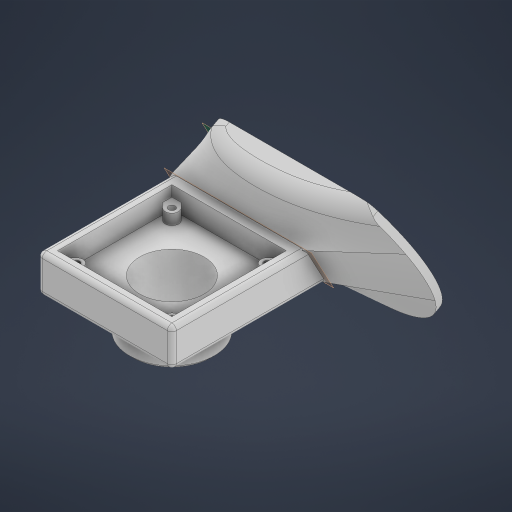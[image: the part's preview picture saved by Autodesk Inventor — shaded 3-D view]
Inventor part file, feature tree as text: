
AUTODESK INVENTOR PART (.ipt)
format: ipt  version: 2023 (Build 270158000, 158)  size: 586,752 bytes
history: native  units: in
note: dims shown in document units (in); Inventor stores cm internally (conversion verified against a paired STEP export)
features: sketch x10, extrude x7, hole x3, fillet x3, plane x2, chamfer x2, other x2, projected_geometry x2, loft x1
ambient origin geometry x8: Origin, YZ Plane, XZ Plane, XY Plane, X Axis, Y Axis, Z Axis, Center Point
bodies: Solid1 (feature_tree)
feature tree (32):
  extrude  "Extrusion1"  Depth=0.525in
  extrude  "Extrusion2"  Depth=0.4252in
  plane  "Work Plane1"
  extrude  "Extrusion3"  Depth=0.6in
  loft  "Loft1"
  extrude  "Extrusion4"  TaperAngle=0.0deg  [1 undecoded]
  hole  "Hole1"  [1 undecoded]
  extrude  "Extrusion5"  Depth=1.1875in
  extrude  "Extrusion6"  Depth=0.1839in
  hole  "Hole2"  [1 undecoded]
  plane  "Work Plane2"
  hole  "Hole3"  [1 undecoded]
  fillet  "Fillet1"  Radius=0.9792in
  chamfer  "Chamfer1"  Distance=0.4466in
  fillet  "Fillet2"  Radius=0.4in
  extrude  "Extrusion7"  Depth=0.15in
  fillet  "Fillet3"  Radius=0.0625in
  chamfer  "Chamfer2"  Distance=0.05in Angle=45.0deg
  sketch  "Sketch1"  dims[d0=1.875in d1=0.525in]
  sketch  "Sketch2"  dims[d2=1.875in d3=0.0in d4=0.4252in]
  sketch  "Sketch3"  dims[d5=1.875in d6=0.0in d7=0.6in]
  other  "Edges1"
  other  "Edges2"
  sketch  "Sketch4"  dims[d9=2.875in d10=0.1in d11=0.0in]
  projected_geometry  "Projected Loop1"
  sketch  "Sketch5"  dims[d12=0.0in d13=90.0deg d14=0.0in d15=90.0deg]
  sketch  "Sketch6"  dims[d16=1.6in d17=0.3in d18=0.0in]
  sketch  "Sketch7"  dims[d19=0.9in d20=0.75in d21=0.119in d22=0.25in d23=0.6871in d24=1.0in d25=0.8108in d26=1.1875in]
  projected_geometry  "Projected Loop2"
  sketch  "Sketch8"  dims[d27=0.5in d28=0.0in d29=0.1839in]
  sketch  "Sketch9"  dims[d30=1.3386in d31=0.15in d32=0.0in]
  sketch  "Sketch10"  dims[d33=0.094in d34=0.75in d35=0.251in d36=0.15in d37=0.6871in d38=1.0in d39=0.8108in d40=0.9792in d41=0.9792in d42=0.4466in d43=0.4in d44=0.65in d45=0.177in d46=0.75in d47=0.313in d48=0.45in d49=0.5635in d50=1.0in d51=0.8108in d52=0.0625in d53=0.05in d54=0.125in d55=45.0deg d56=0.0625in d57=1.0in d58=1.0in d59=0.0in d60=0.25in d61=0.02in d62=0.125in d63=45.0deg]
note: 4 required parameter values undecoded (feature->parameter linkage not recoverable at this tier; creation-order binding heuristic only, values carry confidence <= 0.55)
